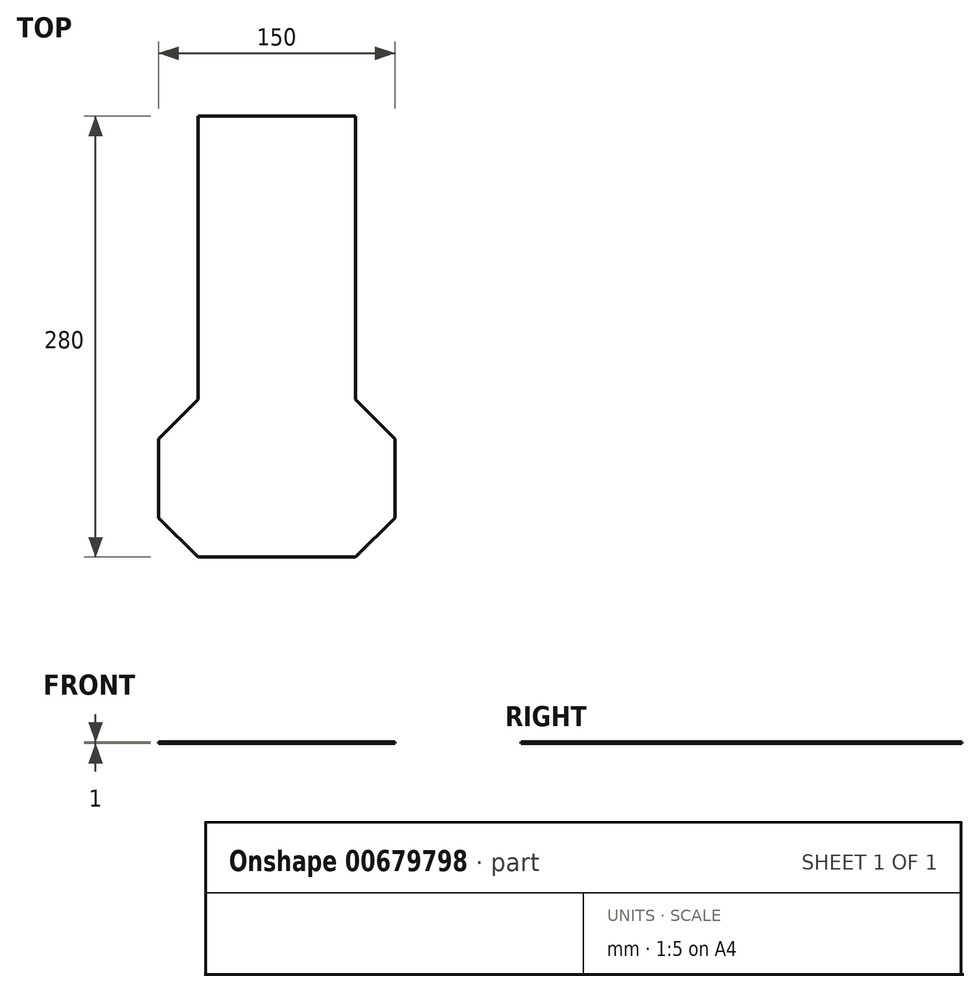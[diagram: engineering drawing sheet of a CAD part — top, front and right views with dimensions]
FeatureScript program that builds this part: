
annotation { "Feature Type Name" : "Feature", "Feature Type Description" : "" }
export const myFeature = defineFeature(function(context is Context, id is Id, definition is map)
    precondition{}
    {
        {
            var Q0;
            Q0=qCreatedBy(makeId("Top.planeOp"),FACE);
            var sketch = newSketch(context, id + "F0", { "sketchPlane" : qUnion([Q0])});
            skLineSegment(sketch, "E0.bottom", {"start": v(50, 80) * mm, "end": v(-50, 80) * mm});
            skLineSegment(sketch, "E0.top", {"start": v(50, -80) * mm, "end": v(-50, -80) * mm});
            skLineSegment(sketch, "E0.left", {"start": v(50, 80) * mm, "end": v(50, -80) * mm});
            skLineSegment(sketch, "E0.right", {"start": v(-50, 80) * mm, "end": v(-50, -80) * mm});
            skPoint(sketch, "E0.middle", {"position": v(0, 0) * mm});
            skLineSegment(sketch, "E1", {"start": v(-50, -80) * mm, "end": v(-50, -100) * mm});
            skLineSegment(sketch, "E2", {"start": v(-50, -100) * mm, "end": v(50, -100) * mm});
            skLineSegment(sketch, "E3", {"start": v(50, -100) * mm, "end": v(50, -80) * mm});
            skLineSegment(sketch, "E4", {"start": v(-50, -200) * mm, "end": v(50, -200) * mm});
            skLineSegment(sketch, "E5", {"start": v(-50, -200) * mm, "end": v(-75, -175) * mm});
            skLineSegment(sketch, "E6", {"start": v(-50, -100) * mm, "end": v(-75, -125) * mm});
            skLineSegment(sketch, "E7", {"start": v(-75, -175) * mm, "end": v(-75, -125) * mm});
            skLineSegment(sketch, "E8.MirrorCS", {"start": v(50, -100) * mm, "end": v(75, -125) * mm});
            skLineSegment(sketch, "E9.MirrorCS", {"start": v(75, -175) * mm, "end": v(75, -125) * mm});
            skLineSegment(sketch, "E10.MirrorCS", {"start": v(50, -200) * mm, "end": v(75, -175) * mm});
            skLineSegment(sketch, "E11", {"start": v(-50, -200) * mm, "end": v(-50, -100) * mm});
            skLineSegment(sketch, "E12", {"start": v(50, -100) * mm, "end": v(50, -200) * mm});
            skSolve(sketch);
        }
        {
            var Q0;
            Q0 = qSketchRegion(id + "F0", true);
            extrude(context, id + "F1", {"entities" : qUnion([Q0]), "oppositeDirection" : true, "depth" : 1 * mm, "offsetDistance" : 25 * mm});
        }
    });
